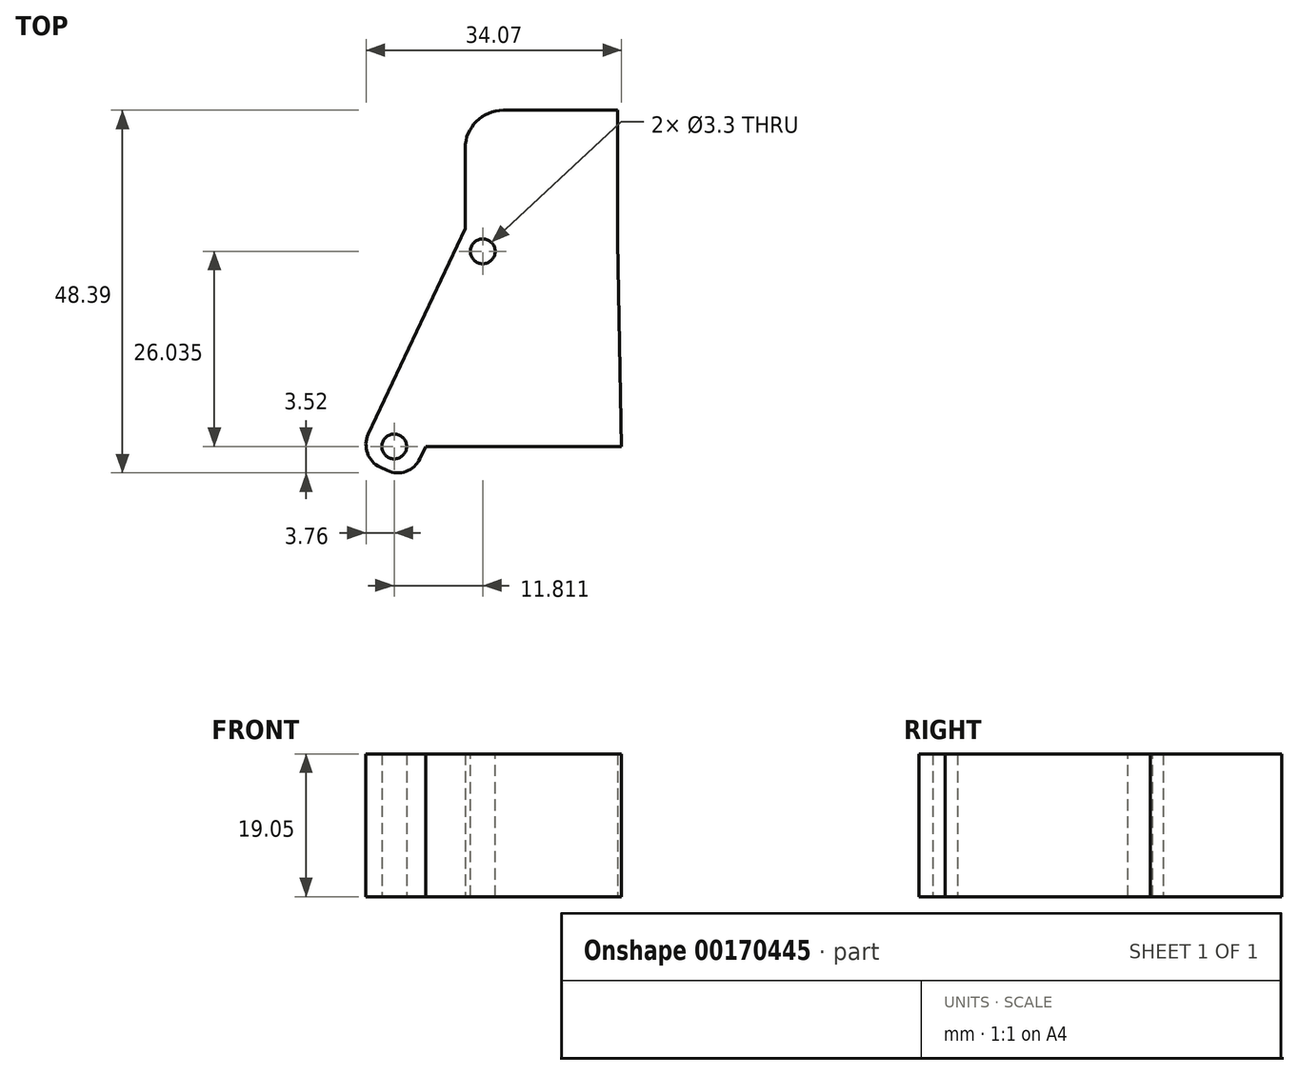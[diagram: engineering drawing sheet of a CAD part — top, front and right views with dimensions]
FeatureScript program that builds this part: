
annotation { "Feature Type Name" : "Feature", "Feature Type Description" : "" }
export const myFeature = defineFeature(function(context is Context, id is Id, definition is map)
    precondition{}
    {
        {
            var Q0;
            Q0=qCreatedBy(makeId("Top.planeOp"),FACE);
            var sketch = newSketch(context, id + "F0", { "sketchPlane" : qUnion([Q0])});
            skLineSegment(sketch, "E0", {"start": v(-4.85, -1.36) * mm, "end": v(9.47, 29.05) * mm});
            skLineSegment(sketch, "E1", {"start": v(9.47, 29.05) * mm, "end": v(9.47, 44.87) * mm});
            skLineSegment(sketch, "E2", {"start": v(9.47, 44.87) * mm, "end": v(17.1, 44.87) * mm});
            skLineSegment(sketch, "E3", {"start": v(17.1, 44.87) * mm, "end": v(17.1, 27.34) * mm});
            skLineSegment(sketch, "E4", {"start": v(-4.85, -1.36) * mm, "end": v(2.04, -4.61) * mm});
            skLineSegment(sketch, "E5", {"start": v(2.04, -4.61) * mm, "end": v(17.1, 27.34) * mm});
            skCircle(sketch, "E6", {"center": v(0, 0) * mm, "radius": 1.65 * mm});
            skSolve(sketch);
        }
        {
            var Q0;
            Q0 = qSketchRegion(id + "F0", true);
            extrude(context, id + "F1", {"entities" : qUnion([Q0]), "depth" : 19.05 * mm});
        }
        {
            var Q0;
            Q0=makeQuery(id+"F1.opExtrude","CAP_FACE",FACE,{"disambiguationData":[OSD([sQuery(id+"F0.wireOp",EDGE,"E0"),sQuery(id+"F0.wireOp",EDGE,"E1"),sQuery(id+"F0.wireOp",EDGE,"E2"),sQuery(id+"F0.wireOp",EDGE,"E3"),sQuery(id+"F0.wireOp",EDGE,"E4"),sQuery(id+"F0.wireOp",EDGE,"E5")])],"isStart":false});
            var sketch = newSketch(context, id + "F2", { "sketchPlane" : qUnion([Q0])});
            skCircle(sketch, "E7", {"center": v(0, 0) * mm, "radius": 1.65 * mm});
            skCircle(sketch, "E8", {"center": v(11.81, 26.04) * mm, "radius": 1.65 * mm});
            skSolve(sketch);
        }
        {
            var Q0;
            Q0 = qSketchRegion(id + "F2", true);
            var Q1;
            Q1=makeQuery(id+"F1.opExtrude","CAP_FACE",FACE,{"disambiguationData":[OSD([sQuery(id+"F0.wireOp",EDGE,"E0"),sQuery(id+"F0.wireOp",EDGE,"E1"),sQuery(id+"F0.wireOp",EDGE,"E2"),sQuery(id+"F0.wireOp",EDGE,"E3"),sQuery(id+"F0.wireOp",EDGE,"E4"),sQuery(id+"F0.wireOp",EDGE,"E5")])],"isStart":true});
            extrude(context, id + "F3", {"entities" : qUnion([Q0]), "operationType" : NewBodyOperationType.REMOVE, "endBound" : BoundingType.UP_TO_SURFACE, "oppositeDirection" : true, "endBoundEntityFace" : qUnion([Q1]), "depth" : 25.4 * mm});
        }
        {
            var Q0;
            Q0=makeQuery(id+"F1.opExtrude","CAP_FACE",FACE,{"disambiguationData":[OSD([sQuery(id+"F0.wireOp",EDGE,"E0"),sQuery(id+"F0.wireOp",EDGE,"E1"),sQuery(id+"F0.wireOp",EDGE,"E2"),sQuery(id+"F0.wireOp",EDGE,"E3"),sQuery(id+"F0.wireOp",EDGE,"E4"),sQuery(id+"F0.wireOp",EDGE,"E5")])],"isStart":false});
            var sketch = newSketch(context, id + "F4", { "sketchPlane" : qUnion([Q0])});
            skLineSegment(sketch, "E9", {"start": v(17.1, 27.6) * mm, "end": v(16.74, 27.95) * mm});
            skLineSegment(sketch, "E10", {"start": v(16.74, 27.95) * mm, "end": v(17.1, 28.31) * mm});
            skLineSegment(sketch, "E11", {"start": v(17.1, 27.6) * mm, "end": v(17.1, 28.31) * mm});
            skLineSegment(sketch, "E12.0.1.0", {"start": v(17.1, 28.61) * mm, "end": v(17.1, 29.33) * mm});
            skLineSegment(sketch, "E12.0.1.1", {"start": v(16.74, 28.97) * mm, "end": v(17.1, 29.33) * mm});
            skLineSegment(sketch, "E12.0.1.2", {"start": v(17.1, 28.61) * mm, "end": v(16.74, 28.97) * mm});
            skLineSegment(sketch, "E12.0.2.0", {"start": v(17.1, 29.63) * mm, "end": v(17.1, 30.34) * mm});
            skLineSegment(sketch, "E12.0.2.1", {"start": v(16.74, 29.99) * mm, "end": v(17.1, 30.34) * mm});
            skLineSegment(sketch, "E12.0.2.2", {"start": v(17.1, 29.63) * mm, "end": v(16.74, 29.99) * mm});
            skLineSegment(sketch, "E12.0.3.0", {"start": v(17.1, 30.64) * mm, "end": v(17.1, 31.36) * mm});
            skLineSegment(sketch, "E12.0.3.1", {"start": v(16.74, 31) * mm, "end": v(17.1, 31.36) * mm});
            skLineSegment(sketch, "E12.0.3.2", {"start": v(17.1, 30.64) * mm, "end": v(16.74, 31) * mm});
            skLineSegment(sketch, "E12.0.4.0", {"start": v(17.1, 31.66) * mm, "end": v(17.1, 32.38) * mm});
            skLineSegment(sketch, "E12.0.4.1", {"start": v(16.74, 32.02) * mm, "end": v(17.1, 32.38) * mm});
            skLineSegment(sketch, "E12.0.4.2", {"start": v(17.1, 31.66) * mm, "end": v(16.74, 32.02) * mm});
            skLineSegment(sketch, "E12.direction2", {"start": v(17.1, 27.6) * mm, "end": v(17.1, 28.61) * mm, "construction": true});
            skLineSegment(sketch, "E13.0.0.5", {"start": v(17.1, 32.67) * mm, "end": v(17.1, 33.4) * mm});
            skLineSegment(sketch, "E13.3.0.5", {"start": v(16.74, 33.03) * mm, "end": v(17.1, 33.4) * mm});
            skLineSegment(sketch, "E13.6.0.5", {"start": v(17.1, 32.67) * mm, "end": v(16.74, 33.03) * mm});
            skLineSegment(sketch, "E13.0.0.6", {"start": v(17.1, 33.7) * mm, "end": v(17.1, 34.4) * mm});
            skLineSegment(sketch, "E13.3.0.6", {"start": v(16.74, 34.05) * mm, "end": v(17.1, 34.4) * mm});
            skLineSegment(sketch, "E13.6.0.6", {"start": v(17.1, 33.7) * mm, "end": v(16.74, 34.05) * mm});
            skLineSegment(sketch, "E13.0.0.7", {"start": v(17.1, 34.7) * mm, "end": v(17.1, 35.42) * mm});
            skLineSegment(sketch, "E13.3.0.7", {"start": v(16.74, 35.07) * mm, "end": v(17.1, 35.42) * mm});
            skLineSegment(sketch, "E13.6.0.7", {"start": v(17.1, 34.7) * mm, "end": v(16.74, 35.07) * mm});
            skLineSegment(sketch, "E13.0.0.8", {"start": v(17.1, 35.72) * mm, "end": v(17.1, 36.44) * mm});
            skLineSegment(sketch, "E13.3.0.8", {"start": v(16.74, 36.08) * mm, "end": v(17.1, 36.44) * mm});
            skLineSegment(sketch, "E13.6.0.8", {"start": v(17.1, 35.72) * mm, "end": v(16.74, 36.08) * mm});
            skLineSegment(sketch, "E13.0.0.9", {"start": v(17.1, 36.74) * mm, "end": v(17.1, 37.46) * mm});
            skLineSegment(sketch, "E13.3.0.9", {"start": v(16.74, 37.1) * mm, "end": v(17.1, 37.46) * mm});
            skLineSegment(sketch, "E13.6.0.9", {"start": v(17.1, 36.74) * mm, "end": v(16.74, 37.1) * mm});
            skLineSegment(sketch, "E14.0.0.10", {"start": v(17.1, 37.75) * mm, "end": v(17.1, 38.47) * mm});
            skLineSegment(sketch, "E14.3.0.10", {"start": v(16.74, 38.11) * mm, "end": v(17.1, 38.47) * mm});
            skLineSegment(sketch, "E14.6.0.10", {"start": v(17.1, 37.75) * mm, "end": v(16.74, 38.11) * mm});
            skLineSegment(sketch, "E14.0.0.11", {"start": v(17.1, 38.77) * mm, "end": v(17.1, 39.49) * mm});
            skLineSegment(sketch, "E14.3.0.11", {"start": v(16.74, 39.13) * mm, "end": v(17.1, 39.49) * mm});
            skLineSegment(sketch, "E14.6.0.11", {"start": v(17.1, 38.77) * mm, "end": v(16.74, 39.13) * mm});
            skLineSegment(sketch, "E14.0.0.12", {"start": v(17.1, 39.79) * mm, "end": v(17.1, 40.5) * mm});
            skLineSegment(sketch, "E14.3.0.12", {"start": v(16.74, 40.15) * mm, "end": v(17.1, 40.5) * mm});
            skLineSegment(sketch, "E14.6.0.12", {"start": v(17.1, 39.79) * mm, "end": v(16.74, 40.15) * mm});
            skLineSegment(sketch, "E14.0.0.13", {"start": v(17.1, 40.8) * mm, "end": v(17.1, 41.52) * mm});
            skLineSegment(sketch, "E14.3.0.13", {"start": v(16.74, 41.16) * mm, "end": v(17.1, 41.52) * mm});
            skLineSegment(sketch, "E14.6.0.13", {"start": v(17.1, 40.8) * mm, "end": v(16.74, 41.16) * mm});
            skLineSegment(sketch, "E14.0.0.14", {"start": v(17.1, 41.82) * mm, "end": v(17.1, 42.54) * mm});
            skLineSegment(sketch, "E14.3.0.14", {"start": v(16.74, 42.18) * mm, "end": v(17.1, 42.54) * mm});
            skLineSegment(sketch, "E14.6.0.14", {"start": v(17.1, 41.82) * mm, "end": v(16.74, 42.18) * mm});
            skLineSegment(sketch, "E15.0.0.15", {"start": v(17.1, 42.83) * mm, "end": v(17.1, 43.55) * mm});
            skLineSegment(sketch, "E15.3.0.15", {"start": v(16.74, 43.2) * mm, "end": v(17.1, 43.55) * mm});
            skLineSegment(sketch, "E15.6.0.15", {"start": v(17.1, 42.83) * mm, "end": v(16.74, 43.2) * mm});
            skLineSegment(sketch, "E15.0.0.16", {"start": v(17.1, 43.85) * mm, "end": v(17.1, 44.57) * mm});
            skLineSegment(sketch, "E15.3.0.16", {"start": v(16.74, 44.2) * mm, "end": v(17.1, 44.57) * mm});
            skLineSegment(sketch, "E15.6.0.16", {"start": v(17.1, 43.85) * mm, "end": v(16.74, 44.2) * mm});
            skSolve(sketch);
        }
        {
            var Q0;
            Q0=makeQuery(id+"F1.opExtrude","SWEPT_EDGE",EDGE,{"disambiguationData":[OSD([sQuery(id+"F0.wireOp",EDGE,"E1"),sQuery(id+"F0.wireOp",EDGE,"E2")])]});
            fillet(context, id + "F5", {"entities" : qUnion([Q0]), "radius" : 5.08 * mm, "tangentPropagation" : true, "allowEdgeOverflow" : false});
        }
        {
            var Q0;
            Q0=makeQuery(id+"F1.opExtrude","SWEPT_EDGE",EDGE,{"disambiguationData":[OSD([sQuery(id+"F0.wireOp",EDGE,"E0"),sQuery(id+"F0.wireOp",EDGE,"E4")])]});
            var Q1;
            Q1=makeQuery(id+"F1.opExtrude","SWEPT_EDGE",EDGE,{"disambiguationData":[OSD([sQuery(id+"F0.wireOp",EDGE,"E4"),sQuery(id+"F0.wireOp",EDGE,"E5")])]});
            fillet(context, id + "F6", {"entities" : qUnion([Q0, Q1]), "radius" : 3.3 * mm, "tangentPropagation" : true, "allowEdgeOverflow" : false});
        }
        {
            var Q0;
            Q0=makeQuery(id+"F1.opExtrude","SWEPT_FACE",FACE,{"disambiguationData":[OSD([sQuery(id+"F0.wireOp",EDGE,"E3")])]});
            extrude(context, id + "F7", {"entities" : qUnion([Q0]), "operationType" : NewBodyOperationType.ADD, "depth" : 12.7 * mm});
        }
        {
            var Q0;
            {var subQ0=sQuery(id+"F0.wireOp",EDGE,"E3");Q0=makeQuery(id+"F7.boolean.opBoolean","MERGE",FACE,{"derivedFrom":[makeQuery(id+"F1.opExtrude","CAP_FACE",FACE,{"disambiguationData":[OSD([sQuery(id+"F0.wireOp",EDGE,"E0"),sQuery(id+"F0.wireOp",EDGE,"E1"),sQuery(id+"F0.wireOp",EDGE,"E2"),subQ0,sQuery(id+"F0.wireOp",EDGE,"E4"),sQuery(id+"F0.wireOp",EDGE,"E5"),sQuery(id+"F0.wireOp",EDGE,"E6")])],"isStart":false}),makeQuery(id+"F7.opExtrude","SWEPT_FACE",FACE,{"disambiguationData":[OSD([subQ0]),TDD([makeQuery(id+"F1.opExtrude","CAP_EDGE",EDGE,{"disambiguationData":[OSD([subQ0])],"isStart":false})])]})]});}
            var sketch = newSketch(context, id + "F8", { "sketchPlane" : qUnion([Q0])});
            skLineSegment(sketch, "E16", {"start": v(29.8, 27.34) * mm, "end": v(30.31, 0) * mm});
            skLineSegment(sketch, "E17", {"start": v(30.31, 0) * mm, "end": v(4.21, 0) * mm});
            skLineSegment(sketch, "E18", {"start": v(4.21, 0) * mm, "end": v(17.1, 27.34) * mm});
            skLineSegment(sketch, "E19", {"start": v(17.1, 27.34) * mm, "end": v(29.8, 27.34) * mm});
            skSolve(sketch);
        }
        {
            var Q0;
            Q0 = qSketchRegion(id + "F8", true);
            var Q1;
            {var subQ0=sQuery(id+"F0.wireOp",EDGE,"E3");Q1=makeQuery(id+"F7.boolean.opBoolean","MERGE",FACE,{"derivedFrom":[makeQuery(id+"F1.opExtrude","CAP_FACE",FACE,{"disambiguationData":[OSD([sQuery(id+"F0.wireOp",EDGE,"E0"),sQuery(id+"F0.wireOp",EDGE,"E1"),sQuery(id+"F0.wireOp",EDGE,"E2"),subQ0,sQuery(id+"F0.wireOp",EDGE,"E4"),sQuery(id+"F0.wireOp",EDGE,"E5"),sQuery(id+"F0.wireOp",EDGE,"E6")])],"isStart":true}),makeQuery(id+"F7.opExtrude","SWEPT_FACE",FACE,{"disambiguationData":[OSD([subQ0]),TDD([makeQuery(id+"F1.opExtrude","CAP_EDGE",EDGE,{"disambiguationData":[OSD([subQ0])],"isStart":true})])]})]});}
            extrude(context, id + "F9", {"entities" : qUnion([Q0]), "operationType" : NewBodyOperationType.ADD, "endBound" : BoundingType.UP_TO_SURFACE, "oppositeDirection" : true, "endBoundEntityFace" : qUnion([Q1]), "depth" : 25.4 * mm});
        }
    });
